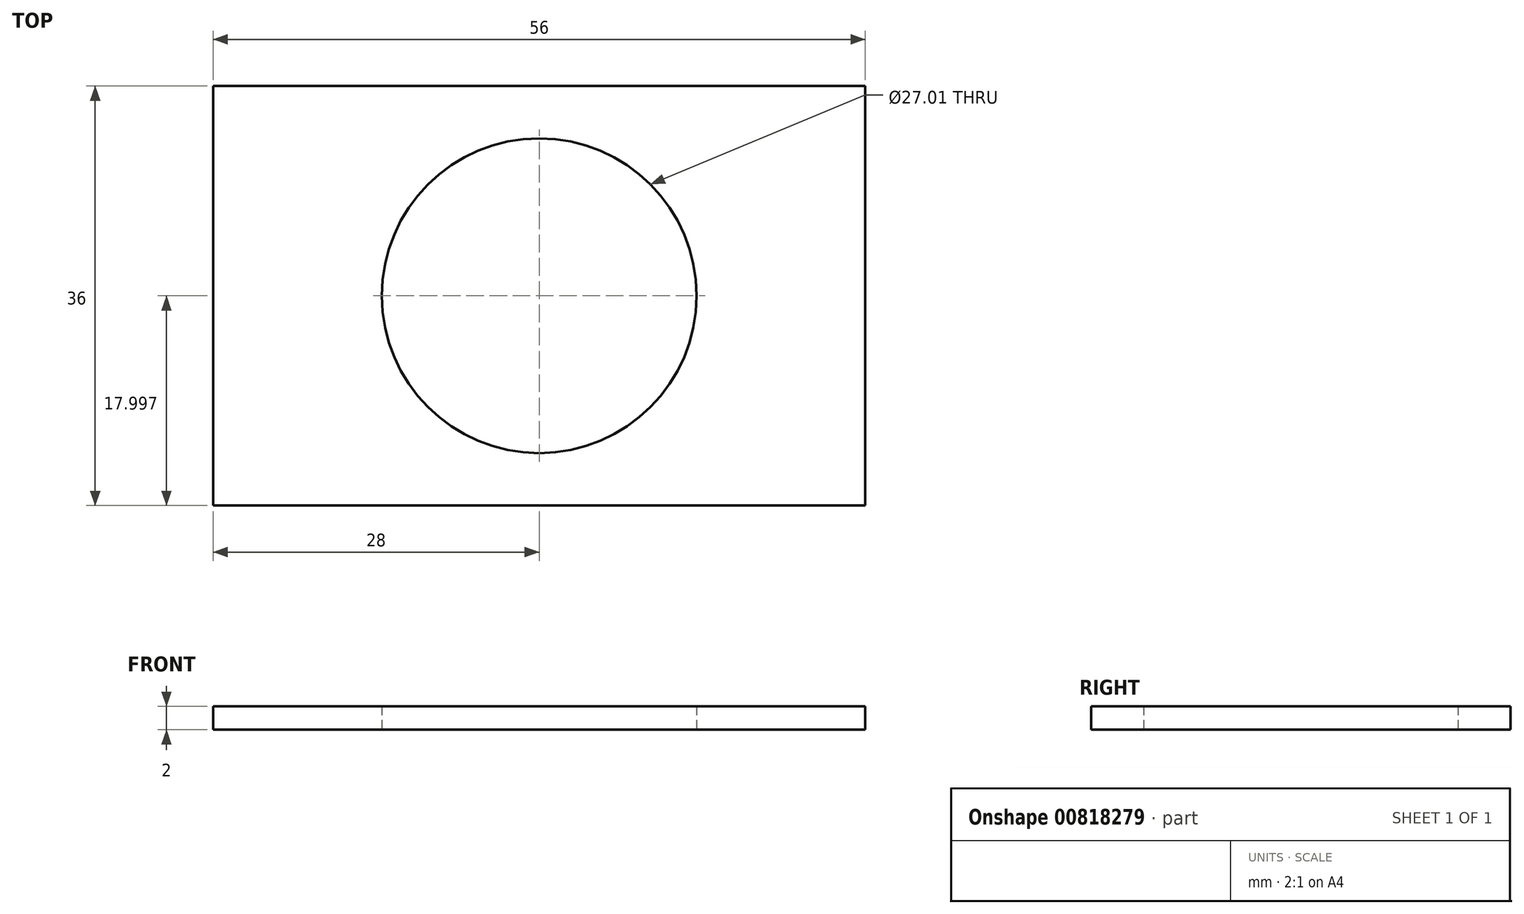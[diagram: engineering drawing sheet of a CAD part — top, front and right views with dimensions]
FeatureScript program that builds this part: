
annotation { "Feature Type Name" : "Feature", "Feature Type Description" : "" }
export const myFeature = defineFeature(function(context is Context, id is Id, definition is map)
    precondition{}
    {
        {
            var Q0;
            Q0=qCreatedBy(makeId("Top.planeOp"),FACE);
            var sketch = newSketch(context, id + "F0", { "sketchPlane" : qUnion([Q0])});
            skLineSegment(sketch, "E0.bottom", {"start": v(-56, 51.88) * mm, "end": v(0, 51.88) * mm});
            skLineSegment(sketch, "E0.top", {"start": v(-56, 15.88) * mm, "end": v(0, 15.88) * mm});
            skLineSegment(sketch, "E0.left", {"start": v(-56, 51.88) * mm, "end": v(-56, 15.88) * mm});
            skLineSegment(sketch, "E0.right", {"start": v(0, 51.88) * mm, "end": v(0, 15.88) * mm});
            skCircle(sketch, "E1", {"center": v(-28, 33.88) * mm, "radius": 13.5 * mm});
            skSolve(sketch);
        }
        {
            var Q0;
            Q0=makeQuery(id+"F0.imprint","IMPRINT",FACE,{"disambiguationData":[TD([[makeQuery(id+"F0.imprint","IMPRINT",EDGE,{"derivedFrom":sQuery(id+"F0.wireOp",EDGE,"E0.bottom")}),-1.0]])]});
            extrude(context, id + "F1", {"entities" : qUnion([Q0]), "depth" : 2 * mm, "offsetDistance" : 25 * mm});
        }
    });
